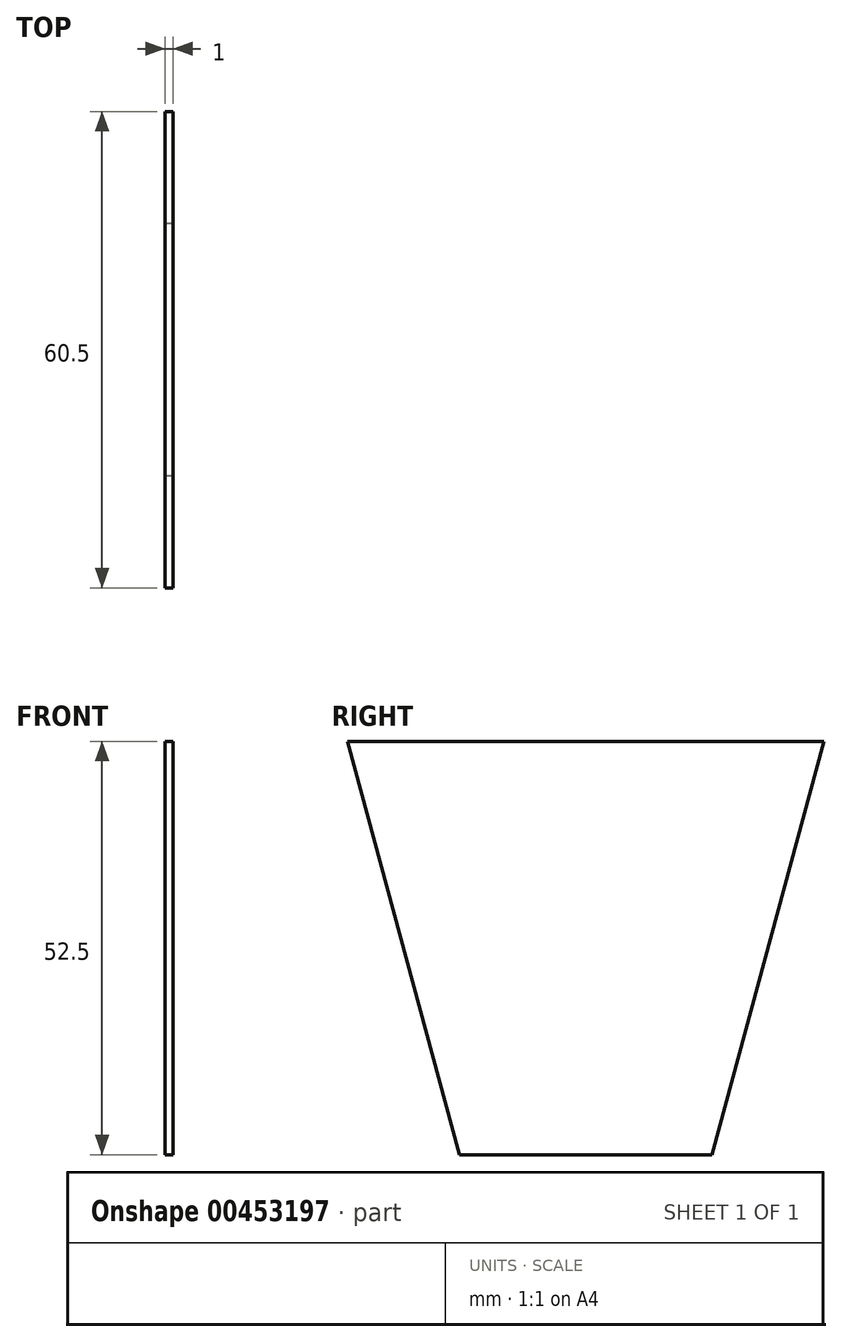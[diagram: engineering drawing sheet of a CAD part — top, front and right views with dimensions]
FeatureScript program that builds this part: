
annotation { "Feature Type Name" : "Feature", "Feature Type Description" : "" }
export const myFeature = defineFeature(function(context is Context, id is Id, definition is map)
    precondition{}
    {
        {
            var Q0;
            Q0=qCreatedBy(makeId("Right.planeOp"),FACE);
            var sketch = newSketch(context, id + "F0", { "sketchPlane" : qUnion([Q0])});
            skLineSegment(sketch, "E0", {"start": v(0, 0) * mm, "end": v(16.05, 0) * mm});
            skPoint(sketch, "E1.endSnap0", {"position": v(8.02, 0) * mm});
            skLineSegment(sketch, "E2", {"start": v(-16.04, 0) * mm, "end": v(0, 0) * mm});
            skLineSegment(sketch, "E3", {"start": v(0, 52.5) * mm, "end": v(30.25, 52.5) * mm});
            skPoint(sketch, "E4.endSnap0", {"position": v(15.12, 52.5) * mm});
            skLineSegment(sketch, "E5", {"start": v(-30.25, 52.5) * mm, "end": v(0, 52.5) * mm});
            skLineSegment(sketch, "E6", {"start": v(30.25, 52.5) * mm, "end": v(16.05, 0) * mm});
            skLineSegment(sketch, "E7", {"start": v(-30.25, 52.5) * mm, "end": v(-16.04, 0) * mm});
            skSolve(sketch);
        }
        {
            var Q0;
            Q0=qSketchRegion(id+"F0",true);
            var Q1;
            {var subQ1=sQuery(id+"F0.wireOp",EDGE,"E0");Q1=makeQuery(id+"F0.imprint","IMPRINT",FACE,{"disambiguationData":[TD([[makeQuery(id+"F0.imprint","IMPRINT",EDGE,{"derivedFrom":subQ1}),1.0]])]});}
            extrude(context, id + "F1", {"entities" : qUnion([Q0, Q1]), "depth" : 1 * mm});
        }
    });
